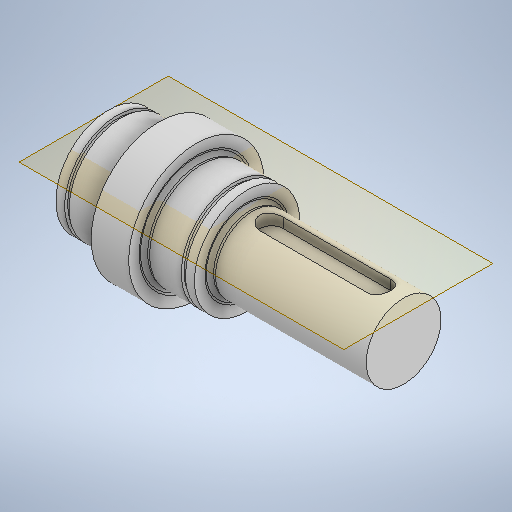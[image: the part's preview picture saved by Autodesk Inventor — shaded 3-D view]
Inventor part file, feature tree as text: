
AUTODESK INVENTOR PART (.ipt)
format: ipt  version: 2025.3 (Build 293356030, 356C)  size: 355,328 bytes
history: native  units: mm
features: sketch x7, revolve x6, plane x1, extrude x1
ambient origin geometry x8: Origin, YZ Plane, XZ Plane, XY Plane, X Axis, Y Axis, Z Axis, Center Point
bodies: Body1 (feature_tree)
feature tree (15):
  revolve  "Umdrehung7"
  revolve  "Umdrehung8"
  revolve  "Umdrehung9"
  revolve  "Umdrehung10"
  revolve  "Umdrehung11"
  plane  "Arbeitsebene2"
  extrude  "Extrusion2"  TaperAngle=0.0deg  [1 undecoded]
  revolve  "Umdrehung12"
  sketch  "Skizze8"  dims[d9=0.0mm d10=0.0mm]
  sketch  "Skizze9"  dims[d11=0.0mm]
  sketch  "Skizze10"  dims[d12=0.0mm]
  sketch  "Skizze11"  dims[d13=0.0mm]
  sketch  "Skizze12"  dims[d14=16.0mm]
  sketch  "Skizze13"  dims[d15=5.0mm d16=0.0mm]
  sketch  "Skizze14"  dims[d17=0.0mm]
note: 1 required parameter value undecoded (feature->parameter linkage not recoverable at this tier; creation-order binding heuristic only, values carry confidence <= 0.55)
